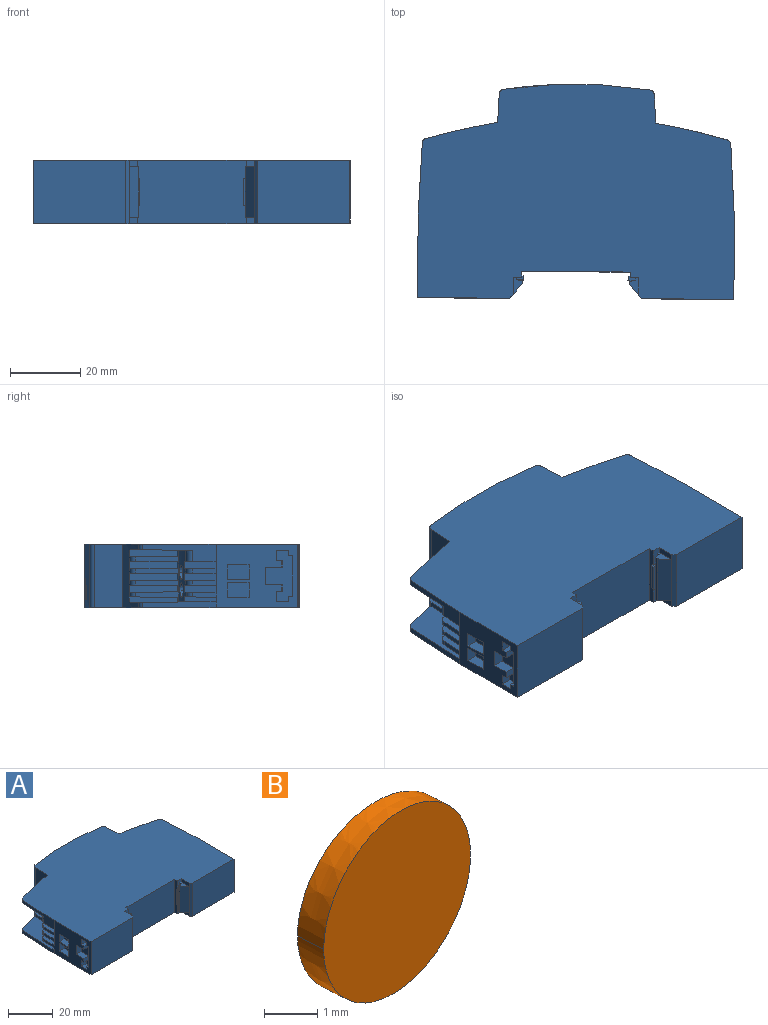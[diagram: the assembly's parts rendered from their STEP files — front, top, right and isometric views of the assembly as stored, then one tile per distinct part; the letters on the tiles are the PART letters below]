
ASSEMBLY  parts=2 mates=1
PART A: 231 faces, bbox 90x61x18 mm
  f0: plane 4.06x4.04mm, normal (-0.25,0.97,0), area 13.3mm2, adj f2,f3
  f1: plane 4.06x4.04mm, normal (-0.25,0.97,0), area 13.3mm2, adj f4,f5
  f2: extruded ~4.8x4.01mm, area 19.5mm2, adj f0,f3,f26
  f3: extruded ~4.8x4.01mm, area 19.5mm2, adj f0,f2,f26
  f4: extruded ~4.79x3.97mm, area 19.2mm2, adj f1,f5,f26
  f5: extruded ~4.79x3.97mm, area 19.2mm2, adj f1,f4,f26
  f6: plane 9.06x2.05mm, normal (-1,0.05,0), area 17.9mm2, adj f26,f31,f32,f33
  f7: plane 9.03x2.05mm, normal (-1,0.05,0), area 17.8mm2, adj f26,f35,f36,f37
  f8: plane 4.13x4.11mm, normal (-0.06,1,0), area 13.3mm2, adj f58,f59
  f9: cylinder r=119mm len=2.3mm, axis (0,0.01,1), area 4.2mm2, adj f10,f24,f26,f60
  f10: plane 14.12x2.3mm, normal (0,0.01,-1), area 26mm2, adj f9,f11,f60,f61,f150
  f11: plane 12.25x1.56mm, normal (-1,0.05,0), area 17.8mm2, adj f10,f12,f26,f61
  f12: plane 14.11x2.3mm, normal (0,0.01,1), area 25.9mm2, adj f11,f13,f61,f62,f150
  f13: cylinder r=119mm len=2.3mm, axis (0,0.01,1), area 4.2mm2, adj f12,f14,f26,f62
  f14: plane 14.09x2.3mm, normal (0,0.01,-1), area 25.9mm2, adj f13,f15,f62,f63,f150
  f15: plane 12.22x1.56mm, normal (-1,0.05,0), area 17.7mm2, adj f14,f16,f26,f63
  f16: plane 14.08x2.3mm, normal (0,0.01,1), area 25.9mm2, adj f15,f25,f63,f64,f150
  f17: cylinder r=119mm len=2.3mm, axis (0,0.01,1), area 3.1mm2, adj f18,f26,f65,f66
  f18: plane 14.18x2.3mm, normal (0,0.01,-1), area 26.1mm2, adj f17,f19,f66,f67,f150
  f19: plane 12.31x1.56mm, normal (-1,0.05,0), area 17.9mm2, adj f18,f20,f26,f67
  f20: plane 14.17x2.3mm, normal (0,0.01,1), area 26.1mm2, adj f19,f21,f67,f68,f150
  f21: cylinder r=119mm len=2.3mm, axis (0,0.01,1), area 4.2mm2, adj f20,f22,f26,f68
  f22: plane 14.15x2.3mm, normal (0,0.01,-1), area 26mm2, adj f21,f23,f68,f69,f150
  f23: plane 12.28x1.56mm, normal (-1,0.05,0), area 17.8mm2, adj f22,f24,f26,f69
  f24: plane 14.14x2.3mm, normal (0,0.01,1), area 26mm2, adj f9,f23,f60,f69,f150
  f25: cylinder r=119mm len=2.3mm, axis (0,0.01,1), area 4.2mm2, adj f16,f26,f64,f71
  f26: cylinder r=119mm len=14.78mm, axis (0,0.01,1), area 92.2mm2, adj f2,f3,f4,f5,f6,f7,f9,f11
  f27: plane 9.09x2.05mm, normal (-1,0.05,0), area 17.9mm2, adj f26,f28,f29,f73
  f28: plane 3x1.9mm, normal (0,1,0.01), area 5.7mm2, adj f27,f29,f73,f74
  f29: plane 9.05x3.46mm, normal (0,0.01,1), area 25.5mm2, adj f26,f27,f28,f30,f74
  f30: cylinder r=2mm len=1.83mm, axis (0,-0.01,-1), area 3.3mm2, adj f26,f29,f31,f74
  f31: plane 9.07x3.47mm, normal (0,0.01,-1), area 25.5mm2, adj f6,f26,f30,f32,f74
  f32: plane 3x1.9mm, normal (0,1,0.01), area 5.7mm2, adj f6,f31,f33,f75
  f33: plane 9.02x3.46mm, normal (0,0.01,1), area 25.4mm2, adj f6,f26,f32,f34,f75
  f34: cylinder r=2mm len=1.83mm, axis (0,-0.01,-1), area 3.3mm2, adj f26,f33,f35,f75
  f35: plane 9.04x3.47mm, normal (0,0.01,-1), area 25.4mm2, adj f7,f26,f34,f36,f75
  f36: plane 3x1.9mm, normal (0,1,0.01), area 5.7mm2, adj f7,f35,f37,f76
  f37: plane 8.99x3.46mm, normal (0,0.01,1), area 25.3mm2, adj f7,f26,f36,f38,f76
  f38: cylinder r=2mm len=1.83mm, axis (0,-0.01,-1), area 3.3mm2, adj f26,f37,f39,f76
  f39: plane 9.01x3.47mm, normal (0,0.01,-1), area 25.3mm2, adj f26,f38,f40,f76,f77
  f40: plane 9x1.44mm, normal (-1,0.05,0), area 12.2mm2, adj f26,f39,f65,f77
  f41: plane 6.1x4.2mm, normal (-1,0,0), area 25.6mm2, adj f78,f79,f80,f81
  f42: plane 14.8x7.7mm, normal (-1,0,0), area 73.2mm2, adj f82,f83,f84,f85,f86,f87,f88,f89
  f43: plane 6.1x4.2mm, normal (-1,0,0), area 25.6mm2, adj f98,f99,f100,f101
  f44: plane 14.4x0.65mm, normal (1,0,0), area 9.4mm2, adj f47,f102,f103,f104
  f45: plane 7.8x1.2mm, normal (0.99,0.14,0), area 9.5mm2, adj f46,f106,f107,f108
  f46: plane 7.8x1.8mm, normal (0,-1,0), area 14mm2, adj f45,f47,f106,f108
  f47: plane 14.4x1.8mm, normal (0.24,0.97,0), area 23.5mm2, adj f44,f46,f56,f102,f104,f105,f106,f108
  f48: plane 7.8x1.2mm, normal (-0.99,0.14,0), area 9.5mm2, adj f49,f109,f110,f111
  f49: plane 7.8x1.8mm, normal (0,-1,0), area 14mm2, adj f48,f51,f109,f111
  f50: plane 14.4x0.65mm, normal (-1,0,0), area 9.4mm2, adj f51,f113,f114,f115
  f51: plane 14.4x1.8mm, normal (-0.24,0.97,0), area 23.5mm2, adj f49,f50,f55,f109,f111,f112,f113,f115
  f52: plane 6.1x4.2mm, normal (1,0,0), area 25.6mm2, adj f116,f117,f118,f119
  f53: plane 14.8x7.7mm, normal (1,0,0), area 73.2mm2, adj f120,f121,f122,f123,f124,f125,f126,f127
  f54: plane 6.1x4.2mm, normal (1,0,0), area 25.6mm2, adj f136,f137,f138,f139
  f55: plane 3.3x0.7mm, normal (-1,0,0), area 2.3mm2, adj f51,f109,f115,f141
  f56: plane 3.3x0.7mm, normal (1,0,0), area 2.3mm2, adj f47,f102,f108,f142
  f57: cylinder r=130mm len=1.51mm, axis (0,0,1), area 0.1mm2, adj f65,f143,f144,f188
  f58: extruded ~4.24x2.22mm, area 12.3mm2, adj f8,f59,f147
  f59: extruded ~4.24x2.22mm, area 12.3mm2, adj f8,f58,f147
  f60: plane 13.7x2.05mm, normal (-1,0,0), area 26.5mm2, adj f9,f10,f24,f150
  f61: cylinder r=2mm len=1.85mm, axis (0,0,-1), area 3.4mm2, adj f10,f11,f12,f150
  f62: plane 13.67x2.05mm, normal (-1,0,0), area 26.4mm2, adj f12,f13,f14,f150
  f63: cylinder r=2mm len=1.85mm, axis (0,0,1), area 3.4mm2, adj f14,f15,f16,f150
  f64: plane 13.64x2.03mm, normal (-1,0,0), area 26.1mm2, adj f16,f25,f71,f150
  f65: plane 24.8x12.81mm, normal (0,0.01,1), area 188.3mm2, adj f17,f26,f40,f57,f66,f77,f143,f144
  f66: plane 13.75x1.57mm, normal (-1,0,0), area 20mm2, adj f17,f18,f65,f150
  f67: cylinder r=2mm len=1.85mm, axis (0,0,1), area 3.4mm2, adj f18,f19,f20,f150
  f68: plane 13.73x2.05mm, normal (-1,0,0), area 26.5mm2, adj f20,f21,f22,f150
  f69: cylinder r=2mm len=1.85mm, axis (0,0,1), area 3.4mm2, adj f22,f23,f24,f150
  f70: cylinder r=130mm len=1.55mm, axis (0,0,1), area 0.1mm2, adj f71,f151,f152,f193
  f71: plane 17.97x12.45mm, normal (0,0.01,-1), area 161.4mm2, adj f25,f26,f64,f70,f72,f150,f151,f152
  f72: cylinder r=2mm len=3.26mm, axis (0,-0.01,-1), area 8mm2, adj f26,f71,f73,f152
  f73: plane 9.1x3.47mm, normal (0,0.01,-1), area 25.6mm2, adj f26,f27,f28,f72,f152
  f74: plane 6.8x3.36mm, normal (-1,0.05,0), area 9.6mm2, adj f28,f29,f30,f31,f153
  f75: plane 6.77x3.36mm, normal (-1,0.05,0), area 9.5mm2, adj f32,f33,f34,f35,f153
  f76: plane 6.74x3.36mm, normal (-1,0.05,0), area 9.5mm2, adj f36,f37,f38,f39,f153
  f77: plane 3x1.28mm, normal (0,1,0.01), area 3.8mm2, adj f39,f40,f65,f153
  f78: plane 6.1x3mm, normal (0,0,-1), area 18.3mm2, adj f41,f79,f81,f153
  f79: plane 4.2x3mm, normal (0,1,0), area 12.6mm2, adj f41,f78,f80,f153
  f80: plane 6.1x3mm, normal (0,0,1), area 18.3mm2, adj f41,f79,f81,f153
  f81: plane 4.2x3mm, normal (0,-1,0), area 12.6mm2, adj f41,f78,f80,f153
  f82: plane 3.35x3mm, normal (0,0,-1), area 10mm2, adj f42,f83,f97,f153
  f83: plane 3x1.6mm, normal (0,1,0), area 4.8mm2, adj f42,f82,f84,f153
  f84: plane 3x1.15mm, normal (0,0,-1), area 3.4mm2, adj f42,f83,f85,f153
  f85: plane 11.6x3mm, normal (0,1,0), area 34.8mm2, adj f42,f84,f86,f153
  f86: plane 3x1.15mm, normal (0,0,1), area 3.4mm2, adj f42,f85,f87,f153
  f87: plane 3x1.6mm, normal (0,1,0), area 4.8mm2, adj f42,f86,f88,f153
  f88: plane 3.35x3mm, normal (0,0,1), area 10mm2, adj f42,f87,f89,f153
  f89: plane 3x3mm, normal (0,-1,0), area 9mm2, adj f42,f88,f90,f153
  f90: plane 3x1.5mm, normal (0,0,-1), area 4.5mm2, adj f42,f89,f91,f153
  f91: plane 3x1.9mm, normal (0,-1,0), area 5.7mm2, adj f42,f90,f92,f153
  f92: plane 4.7x3mm, normal (0,0,1), area 14.1mm2, adj f42,f91,f93,f153
  f93: plane 5x3mm, normal (0,-1,0), area 15mm2, adj f42,f92,f94,f153
  f94: plane 4.7x3mm, normal (0,0,-1), area 14.1mm2, adj f42,f93,f95,f153
  f95: plane 3x1.9mm, normal (0,-1,0), area 5.7mm2, adj f42,f94,f96,f153
  f96: plane 3x1.5mm, normal (0,0,1), area 4.5mm2, adj f42,f95,f97,f153
  f97: plane 3x3mm, normal (0,-1,0), area 9mm2, adj f42,f82,f96,f153
  f98: plane 4.2x3mm, normal (0,1,0), area 12.6mm2, adj f43,f99,f101,f153
  f99: plane 6.1x3mm, normal (0,0,1), area 18.3mm2, adj f43,f98,f100,f153
  f100: plane 4.2x3mm, normal (0,-1,0), area 12.6mm2, adj f43,f99,f101,f153
  f101: plane 6.1x3mm, normal (0,0,-1), area 18.3mm2, adj f43,f98,f100,f153
  f102: plane 4.9x2.6mm, normal (0,0,-1), area 7mm2, adj f44,f47,f56,f103,f142,f156
  f103: plane 14.4x3.1mm, normal (0.77,-0.64,0), area 58.2mm2, adj f44,f102,f104,f156
  f104: plane 4.9x2.6mm, normal (0,0,1), area 7mm2, adj f44,f47,f103,f105,f156,f157
  f105: plane 3.3x0.7mm, normal (1,0,0), area 2.3mm2, adj f47,f104,f106,f157
  f106: plane 2.2x1.2mm, normal (0,0,1), area 1.9mm2, adj f45,f46,f47,f105,f107,f157,f158
  f107: plane 7.8x0.43mm, normal (0,1,0), area 3.4mm2, adj f45,f106,f108,f158
  f108: plane 2.2x1.2mm, normal (0,0,-1), area 1.9mm2, adj f45,f46,f47,f56,f107,f142,f158
  f109: plane 2.2x1.2mm, normal (0,0,-1), area 1.9mm2, adj f48,f49,f51,f55,f110,f141,f160
  f110: plane 7.8x0.43mm, normal (0,1,0), area 3.4mm2, adj f48,f109,f111,f160
  f111: plane 2.2x1.2mm, normal (0,0,1), area 1.9mm2, adj f48,f49,f51,f110,f112,f160,f161
  f112: plane 3.3x0.7mm, normal (-1,0,0), area 2.3mm2, adj f51,f111,f113,f161
  f113: plane 4.9x2.6mm, normal (0,0,1), area 7mm2, adj f50,f51,f112,f114,f161,f162
  f114: plane 14.4x3.1mm, normal (-0.77,-0.64,0), area 58.2mm2, adj f50,f113,f115,f162
  f115: plane 4.9x2.6mm, normal (0,0,-1), area 7mm2, adj f50,f51,f55,f114,f141,f162
  f116: plane 6.1x3mm, normal (0,0,1), area 18.3mm2, adj f52,f117,f119,f182
  f117: plane 4.2x3mm, normal (0,1,0), area 12.6mm2, adj f52,f116,f118,f182
  f118: plane 6.1x3mm, normal (0,0,-1), area 18.3mm2, adj f52,f117,f119,f182
  f119: plane 4.2x3mm, normal (0,-1,0), area 12.6mm2, adj f52,f116,f118,f182
  f120: plane 4.7x3mm, normal (0,0,1), area 14.1mm2, adj f53,f121,f135,f182
  f121: plane 3x1.9mm, normal (0,-1,0), area 5.7mm2, adj f53,f120,f122,f182
  f122: plane 3x1.5mm, normal (0,0,-1), area 4.5mm2, adj f53,f121,f123,f182
  f123: plane 3x3mm, normal (0,-1,0), area 9mm2, adj f53,f122,f124,f182
  f124: plane 3.35x3mm, normal (0,0,1), area 10mm2, adj f53,f123,f125,f182
  f125: plane 3x1.6mm, normal (0,1,0), area 4.8mm2, adj f53,f124,f126,f182
  f126: plane 3x1.15mm, normal (0,0,1), area 3.4mm2, adj f53,f125,f127,f182
  f127: plane 11.6x3mm, normal (0,1,0), area 34.8mm2, adj f53,f126,f128,f182
  f128: plane 3x1.15mm, normal (0,0,-1), area 3.4mm2, adj f53,f127,f129,f182
  f129: plane 3x1.6mm, normal (0,1,0), area 4.8mm2, adj f53,f128,f130,f182
  f130: plane 3.35x3mm, normal (0,0,-1), area 10mm2, adj f53,f129,f131,f182
  f131: plane 3x3mm, normal (0,-1,0), area 9mm2, adj f53,f130,f132,f182
  f132: plane 3x1.5mm, normal (0,0,1), area 4.5mm2, adj f53,f131,f133,f182
  f133: plane 3x1.9mm, normal (0,-1,0), area 5.7mm2, adj f53,f132,f134,f182
  f134: plane 4.7x3mm, normal (0,0,-1), area 14.1mm2, adj f53,f133,f135,f182
  f135: plane 5x3mm, normal (0,-1,0), area 15mm2, adj f53,f120,f134,f182
  f136: plane 6.1x3mm, normal (0,0,1), area 18.3mm2, adj f54,f137,f139,f182
  f137: plane 4.2x3mm, normal (0,1,0), area 12.6mm2, adj f54,f136,f138,f182
  f138: plane 6.1x3mm, normal (0,0,-1), area 18.3mm2, adj f54,f137,f139,f182
  f139: plane 4.2x3mm, normal (0,-1,0), area 12.6mm2, adj f54,f136,f138,f182
  f140: cylinder r=130mm len=1.51mm, axis (0,0,1), area 0.1mm2, adj f178,f187,f188,f215
  f141: plane 5.1x2.4mm, normal (0,-1,0), area 9.6mm2, adj f55,f109,f115,f160,f162,f188
  f142: plane 5.1x2.4mm, normal (0,-1,0), area 9.6mm2, adj f56,f102,f108,f156,f158,f188
  f143: plane 21.04x1.69mm, normal (-1,0.05,0), area 33.8mm2, adj f57,f65,f153,f188
  f144: cylinder r=1.5mm len=1.51mm, axis (0,0,1), area 2.3mm2, adj f57,f65,f150,f188
  f145: plane 12.25x1.56mm, normal (1,0.05,0), area 17.8mm2, adj f169,f170,f191,f226
  f146: cylinder r=1.5mm len=18mm, axis (0,0,-1), area 37mm2, adj f147,f188,f189,f193
  f147: cylinder r=140mm len=41.61mm, axis (0,0,-1), area 751.7mm2, adj f58,f59,f146,f148,f188,f193
  f148: cylinder r=1.5mm len=18mm, axis (0,0,-1), area 37mm2, adj f147,f149,f188,f193
  f149: plane 18x8.04mm, normal (-1,0.05,0), area 144.9mm2, adj f148,f150,f188,f193
  f150: cylinder r=200mm len=20.33mm, axis (0,0,1), area 211.8mm2, adj f10,f12,f14,f16,f18,f20,f22,f24
  f151: cylinder r=1.5mm len=1.55mm, axis (0,0,1), area 2.4mm2, adj f70,f71,f150,f193
  f152: plane 21.04x4.94mm, normal (-1,0.05,0), area 56.5mm2, adj f70,f71,f72,f73,f153,f193
  f153: plane 23.26x18mm, normal (-1,0,0), area 294.1mm2, adj f74,f75,f76,f77,f78,f79,f80,f81
  f154: plane 26.2x18mm, normal (0,-1,0), area 471.6mm2, adj f153,f155,f188,f193
  f155: plane 18x1mm, normal (0.71,-0.71,0), area 25.5mm2, adj f154,f156,f188,f193
  f156: plane 18x5mm, normal (1,0,0), area 19.5mm2, adj f102,f103,f104,f142,f155,f157,f188,f193
  f157: plane 5.1x2.4mm, normal (0,-1,0), area 9.6mm2, adj f104,f105,f106,f156,f158,f193
  f158: plane 18x1.6mm, normal (1,0,0), area 25.7mm2, adj f106,f107,f108,f142,f157,f159,f188,f193
  f159: plane 30.8x18mm, normal (0,-1,0), area 554.4mm2, adj f158,f160,f188,f193
  f160: plane 18x1.6mm, normal (-1,0,0), area 25.7mm2, adj f109,f110,f111,f141,f159,f161,f188,f193
  f161: plane 5.1x2.4mm, normal (0,-1,0), area 9.6mm2, adj f111,f112,f113,f160,f162,f193
  f162: plane 18x5mm, normal (-1,0,0), area 19.5mm2, adj f113,f114,f115,f141,f161,f163,f188,f193
  f163: plane 18x1mm, normal (-0.71,-0.71,0), area 25.5mm2, adj f162,f164,f188,f193
  f164: plane 26.2x18mm, normal (0,-1,0), area 471.6mm2, adj f163,f182,f188,f193
  f165: plane 14.18x2.3mm, normal (0,0.01,-1), area 26.1mm2, adj f185,f186,f195,f196,f224
  f166: plane 14.17x2.3mm, normal (0,0.01,1), area 26.1mm2, adj f184,f185,f196,f197,f224
  f167: plane 14.15x2.3mm, normal (0,0.01,-1), area 26mm2, adj f183,f184,f197,f198,f224
  f168: plane 14.14x2.3mm, normal (0,0.01,1), area 26mm2, adj f183,f192,f198,f199,f224
  f169: plane 14.12x2.3mm, normal (0,0.01,-1), area 26mm2, adj f145,f191,f192,f199,f224
  f170: plane 14.11x2.3mm, normal (0,0.01,1), area 25.9mm2, adj f145,f190,f191,f200,f224
  f171: plane 3x1.9mm, normal (0,1,0.01), area 5.7mm2, adj f172,f201,f202,f203
  f172: plane 6.8x3.36mm, normal (1,0.05,0), area 9.6mm2, adj f171,f182,f203,f204,f205
  f173: plane 3x1.9mm, normal (0,1,0.01), area 5.7mm2, adj f174,f205,f206,f207
  f174: plane 6.77x3.36mm, normal (1,0.05,0), area 9.5mm2, adj f173,f182,f207,f208,f209
  f175: plane 3x1.9mm, normal (0,1,0.01), area 5.7mm2, adj f176,f209,f210,f211
  f176: plane 6.74x3.36mm, normal (1,0.05,0), area 9.5mm2, adj f175,f182,f211,f212,f213
  f177: plane 3x1.28mm, normal (0,1,0.01), area 3.8mm2, adj f182,f213,f214,f215
  f178: plane 21.04x1.69mm, normal (1,0.05,0), area 33.8mm2, adj f140,f182,f188,f215
  f179: plane 4.06x4.04mm, normal (0.25,0.97,0), area 13.3mm2, adj f216,f217
  f180: plane 4.06x4.04mm, normal (0.25,0.97,0), area 13.3mm2, adj f218,f219
  f181: plane 14.09x2.3mm, normal (0,0.01,-1), area 25.9mm2, adj f190,f200,f220,f221,f224
  f182: plane 23.26x18mm, normal (1,0,0), area 294.1mm2, adj f116,f117,f118,f119,f120,f121,f122,f123
  f183: cylinder r=2mm len=1.85mm, axis (0,0,-1), area 3.4mm2, adj f167,f168,f198,f224
  f184: plane 13.73x2.05mm, normal (1,0,0), area 26.5mm2, adj f166,f167,f197,f224
  f185: cylinder r=2mm len=1.85mm, axis (0,0,-1), area 3.4mm2, adj f165,f166,f196,f224
  f186: plane 13.75x1.57mm, normal (1,0,0), area 20mm2, adj f165,f195,f215,f224
  f187: cylinder r=1.5mm len=1.51mm, axis (0,0,1), area 2.3mm2, adj f140,f188,f215,f224
  f188: plane 90x61mm, normal (0,0,-1), area 4565mm2, adj f57,f140,f141,f142,f143,f144,f146,f147
  f189: plane 18x8.04mm, normal (1,0.05,0), area 144.9mm2, adj f146,f188,f193,f224
  f190: plane 13.67x2.05mm, normal (1,0,0), area 26.4mm2, adj f170,f181,f200,f224
  f191: cylinder r=2mm len=1.85mm, axis (0,0,1), area 3.4mm2, adj f145,f169,f170,f224
  f192: plane 13.7x2.05mm, normal (1,0,0), area 26.5mm2, adj f168,f169,f199,f224
  f193: plane 90x61mm, normal (0,0,1), area 4565mm2, adj f70,f146,f147,f148,f149,f150,f151,f152
  f194: cylinder r=130mm len=1.55mm, axis (0,0,1), area 0.1mm2, adj f193,f222,f225,f229
  f195: cylinder r=119mm len=2.3mm, axis (0,0.01,1), area 3.1mm2, adj f165,f186,f215,f226
  f196: plane 12.31x1.56mm, normal (1,0.05,0), area 17.9mm2, adj f165,f166,f185,f226
  f197: cylinder r=119mm len=2.3mm, axis (0,0.01,1), area 4.2mm2, adj f166,f167,f184,f226
  f198: plane 12.28x1.56mm, normal (1,0.05,0), area 17.8mm2, adj f167,f168,f183,f226
  f199: cylinder r=119mm len=2.3mm, axis (0,0.01,1), area 4.2mm2, adj f168,f169,f192,f226
  f200: cylinder r=119mm len=2.3mm, axis (0,0.01,1), area 4.2mm2, adj f170,f181,f190,f226
  f201: plane 9.1x3.47mm, normal (0,0.01,-1), area 25.6mm2, adj f171,f202,f222,f223,f226
  f202: plane 9.09x2.05mm, normal (1,0.05,0), area 17.9mm2, adj f171,f201,f203,f226
  f203: plane 9.05x3.46mm, normal (0,0.01,1), area 25.5mm2, adj f171,f172,f202,f204,f226
  f204: cylinder r=2mm len=1.83mm, axis (0,0.01,1), area 3.3mm2, adj f172,f203,f205,f226
  f205: plane 9.07x3.47mm, normal (0,0.01,-1), area 25.5mm2, adj f172,f173,f204,f206,f226
  f206: plane 9.06x2.05mm, normal (1,0.05,0), area 17.9mm2, adj f173,f205,f207,f226
  f207: plane 9.02x3.46mm, normal (0,0.01,1), area 25.4mm2, adj f173,f174,f206,f208,f226
  f208: cylinder r=2mm len=1.83mm, axis (0,0.01,1), area 3.3mm2, adj f174,f207,f209,f226
  f209: plane 9.04x3.47mm, normal (0,0.01,-1), area 25.4mm2, adj f174,f175,f208,f210,f226
  f210: plane 9.03x2.05mm, normal (1,0.05,0), area 17.8mm2, adj f175,f209,f211,f226
  f211: plane 8.99x3.46mm, normal (0,0.01,1), area 25.3mm2, adj f175,f176,f210,f212,f226
  f212: cylinder r=2mm len=1.83mm, axis (0,0.01,1), area 3.3mm2, adj f176,f211,f213,f226
  f213: plane 9.01x3.47mm, normal (0,0.01,-1), area 25.3mm2, adj f176,f177,f212,f214,f226
  f214: plane 9x1.44mm, normal (1,0.05,0), area 12.2mm2, adj f177,f213,f215,f226
  f215: plane 24.8x12.81mm, normal (0,0.01,1), area 188.3mm2, adj f140,f177,f178,f186,f187,f195,f214,f224
  f216: extruded ~4.79x3.97mm, area 19.2mm2, adj f179,f217,f226
  f217: extruded ~4.79x3.97mm, area 19.2mm2, adj f179,f216,f226
  f218: extruded ~4.8x4.01mm, area 19.5mm2, adj f180,f219,f226
  f219: extruded ~4.8x4.01mm, area 19.5mm2, adj f180,f218,f226
  f220: plane 12.22x1.56mm, normal (1,0.05,0), area 17.7mm2, adj f181,f221,f226,f227
  f221: cylinder r=2mm len=1.85mm, axis (0,0,-1), area 3.4mm2, adj f181,f220,f224,f227
  f222: plane 21.04x4.94mm, normal (1,0.05,0), area 56.5mm2, adj f182,f193,f194,f201,f223,f229
  f223: cylinder r=2mm len=3.26mm, axis (0,0.01,1), area 8mm2, adj f201,f222,f226,f229
  f224: cylinder r=200mm len=20.33mm, axis (0,0,1), area 211.8mm2, adj f165,f166,f167,f168,f169,f170,f181,f183
  f225: cylinder r=1.5mm len=1.55mm, axis (0,0,1), area 2.4mm2, adj f193,f194,f224,f229
  f226: cylinder r=119mm len=14.78mm, axis (0,0.01,1), area 92.1mm2, adj f145,f195,f196,f197,f198,f199,f200,f201
  f227: plane 14.08x2.3mm, normal (0,0.01,1), area 25.9mm2, adj f220,f221,f224,f228,f230
  f228: plane 13.64x2.03mm, normal (1,0,0), area 26.1mm2, adj f224,f227,f229,f230
  f229: plane 17.96x12.45mm, normal (0,0.01,-1), area 161.4mm2, adj f194,f222,f223,f224,f225,f226,f228,f230
  f230: cylinder r=119mm len=2.3mm, axis (0,0.01,1), area 4.2mm2, adj f226,f227,f228,f229
PART B: 4 faces, bbox 4.2x0.9x4.1 mm
  f0: plane 4.19x4.15mm, normal (0,1,0), area 13.3mm2, adj f1,f2
  f1: extruded ~4.16x2.05mm, area 3.5mm2, adj f0,f2,f3
  f2: extruded ~4.16x2.05mm, area 3.5mm2, adj f0,f1,f3
  f3: plane 4.13x4.11mm, normal (0.06,-1,0), area 13.3mm2, adj f1,f2
PLACE A rot(axis=(0,0,-1),0.3deg) t=(47.84,-25.04,25.11)mm
PLACE B t=(48.08,-24,25.11)mm
MATE fastened A.f8 <-> B.f3  axis (-0.06,1,0) through (35.19,33.69,20.41)mm
